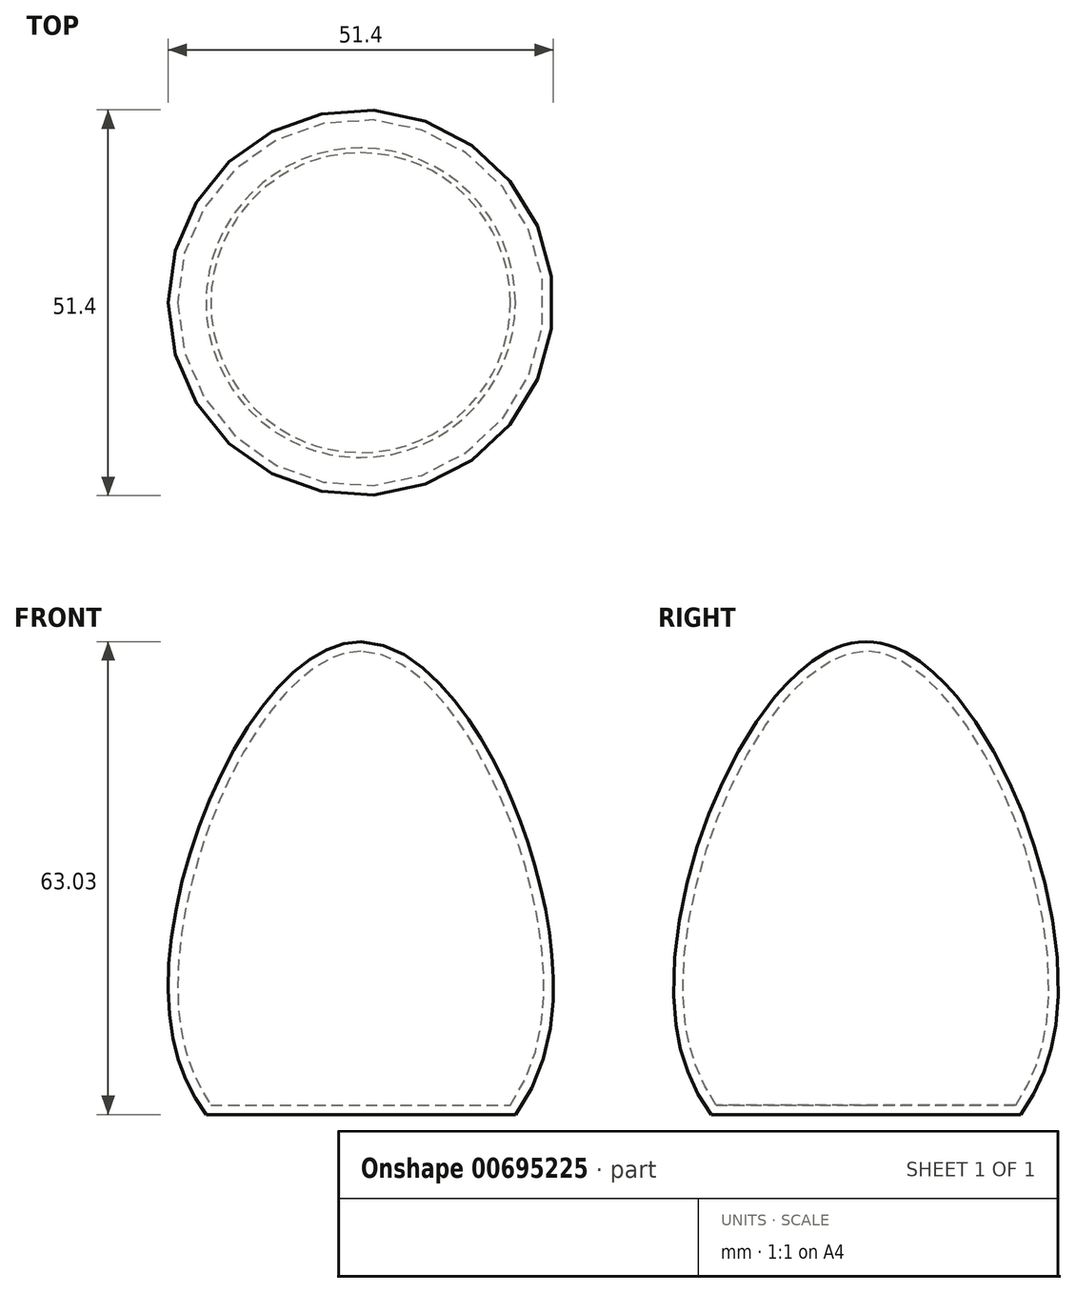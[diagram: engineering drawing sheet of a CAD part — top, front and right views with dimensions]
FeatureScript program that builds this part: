
annotation { "Feature Type Name" : "Feature", "Feature Type Description" : "" }
export const myFeature = defineFeature(function(context is Context, id is Id, definition is map)
    precondition{}
    {
        {
            var Q0;
            Q0=qCreatedBy(makeId("Front.planeOp"),FACE);
            var sketch = newSketch(context, id + "F0", { "sketchPlane" : qUnion([Q0])});
            skLineSegment(sketch, "E0", {"start": v(0, 0) * mm, "end": v(-25.4, 0) * mm, "construction": true});
            skLineSegment(sketch, "E1", {"start": v(0, 0) * mm, "end": v(0, -22.23) * mm});
            skLineSegment(sketch, "E2", {"start": v(0, 0) * mm, "end": v(25.4, 0) * mm, "construction": true});
            skLineSegment(sketch, "E3", {"start": v(0, 0) * mm, "end": v(0, 50.8) * mm});
            skFitSpline(sketch, "E4", {"points": [v(0, 50.8) * mm, v(-25.4, 0) * mm, v(0, -22.23) * mm, v(25.4, 0) * mm, v(0, 50.8) * mm]});
            skLineSegment(sketch, "E5", {"start": v(-20.64, -12.23) * mm, "end": v(20.64, -12.23) * mm});
            skSolve(sketch);
        }
        {
            var Q0;
            {var subQ0=sQuery(id+"F0.wireOp",EDGE,"E3");Q0=makeQuery(id+"F0.imprint","IMPRINT",FACE,{"disambiguationData":[TD([[makeQuery(id+"F0.imprint","IMPRINT",EDGE,{"derivedFrom":subQ0}),1.0]])]});}
            var Q1;
            Q1=sQuery(id+"F0.wireOp",EDGE,"E3");
            revolve(context, id + "F1", {"entities" : qUnion([Q0]), "axis" : qUnion([Q1]), "revolveType" : RevolveType.FULL});
        }
        {
            var Q0;
            Q0=makeQuery(id+"F1.opRevolve","SWEPT_FACE",FACE,{"disambiguationData":[OSD([sQuery(id+"F0.wireOp",EDGE,"E4")])]});
            var Q1;
            Q1=makeQuery(id+"F1.opRevolve","SWEPT_BODY",BODY,{"disambiguationData":[OSD([sQuery(id+"F0.wireOp",EDGE,"E1"),sQuery(id+"F0.wireOp",EDGE,"E3"),sQuery(id+"F0.wireOp",EDGE,"E4"),sQuery(id+"F0.wireOp",EDGE,"E5")])]});
            shell(context, id + "F2", {"isHollow" : true, "entities" : qUnion([Q0]), "parts" : qUnion([Q1]), "thickness" : 1.27 * mm});
        }
    });
